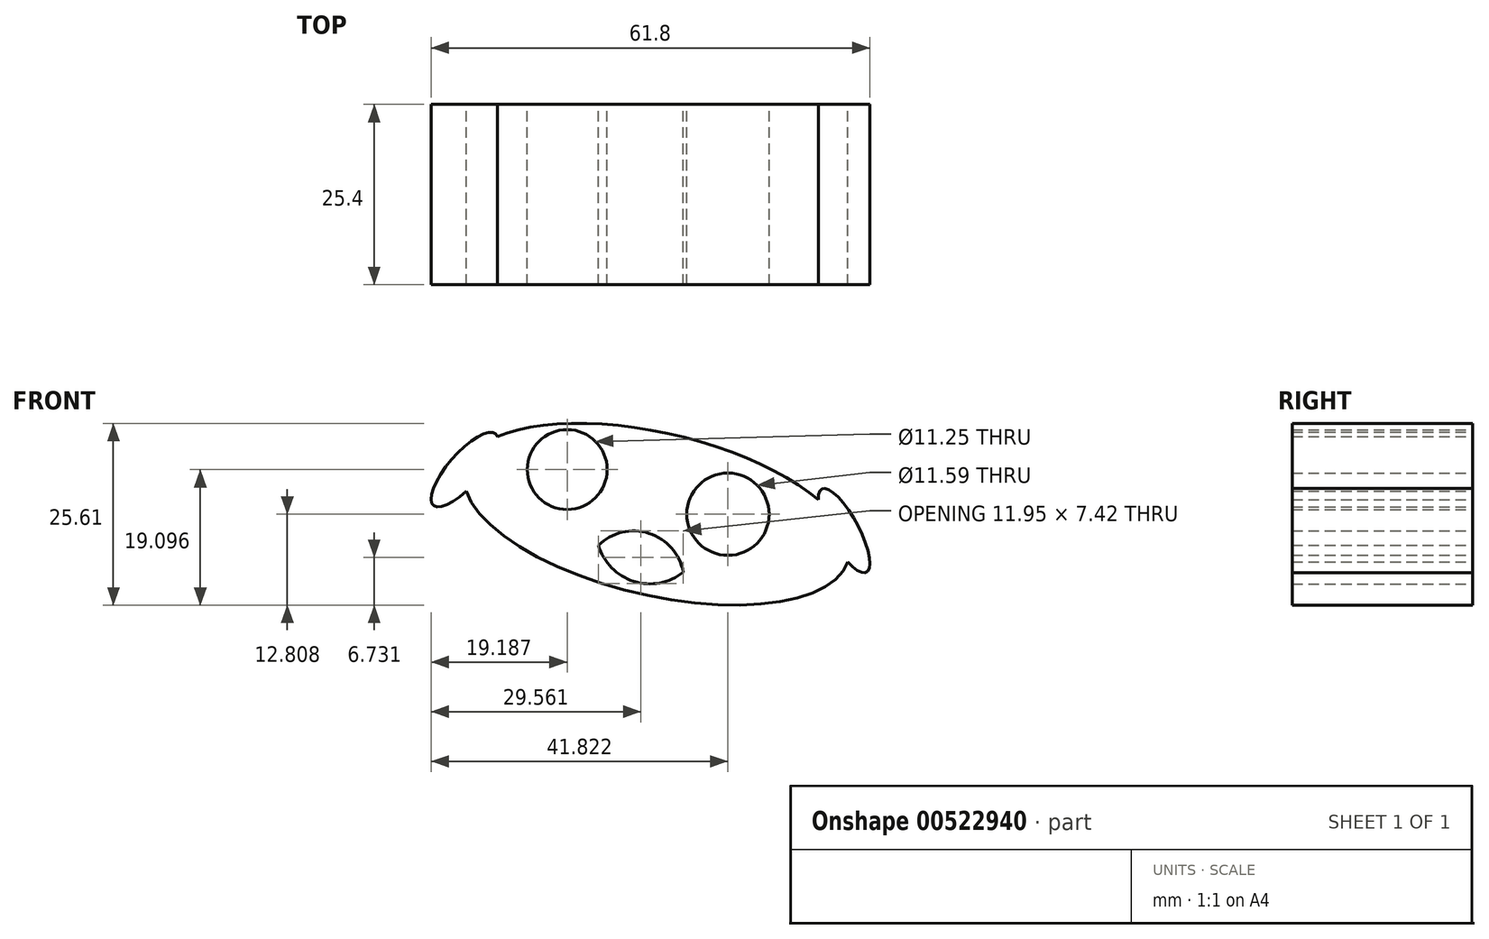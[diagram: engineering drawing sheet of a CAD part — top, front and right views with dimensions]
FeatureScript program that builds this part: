
annotation { "Feature Type Name" : "Feature", "Feature Type Description" : "" }
export const myFeature = defineFeature(function(context is Context, id is Id, definition is map)
    precondition{}
    {
        {
            var Q0;
            Q0=qCreatedBy(makeId("Front.planeOp"),FACE);
            var sketch = newSketch(context, id + "F0", { "sketchPlane" : qUnion([Q0])});
            skEllipse(sketch, "E0", {"center": v(-26.4, 40.4) * mm, "majorRadius": 27.76 * mm, "minorRadius": 11.45 * mm, "majorAxis": v(0.97, -0.23)});
            skCircle(sketch, "E1", {"center": v(-38.98, 46.69) * mm, "radius": 5.62 * mm});
            skCircle(sketch, "E2", {"center": v(-16.35, 40.4) * mm, "radius": 5.8 * mm});
            skArc(sketch, "E3", {"start": v(-22.64, 32.22) * mm, "mid": v(-27.47, 37.7) * mm, "end": v(-34.58, 36) * mm});
            skEllipse(sketch, "E4", {"center": v(0, 38.09) * mm, "majorRadius": 6.65 * mm, "minorRadius": 2.06 * mm, "majorAxis": v(0.47, -0.88)});
            skEllipse(sketch, "E5", {"center": v(-53.44, 46.69) * mm, "majorRadius": 6.68 * mm, "minorRadius": 2.3 * mm, "majorAxis": v(0.66, 0.75)});
            skArc(sketch, "E6", {"start": v(-34.58, 36) * mm, "mid": v(-29.6, 30.95) * mm, "end": v(-22.64, 32.22) * mm});
            skSolve(sketch);
        }
        {
            var Q0;
            Q0 = qSketchRegion(id + "F0", true);
            extrude(context, id + "F1", {"entities" : qUnion([Q0]), "depth" : 25.4 * mm, "offsetDistance" : 25.4 * mm});
        }
    });
